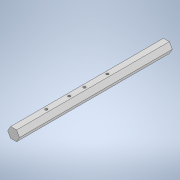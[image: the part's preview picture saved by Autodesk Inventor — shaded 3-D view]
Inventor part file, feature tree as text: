
AUTODESK INVENTOR PART (.ipt)
format: ipt  version: 2022 (Build 260153000, 153)  size: 123,392 bytes
history: native  units: mm
features: extrude x2, sketch x2
ambient origin geometry x8: Origin, YZ Plane, XZ Plane, XY Plane, X Axis, Y Axis, Z Axis, Center Point
bodies: Body1 (feature_tree)
feature tree (4):
  extrude  "Extrusion5"  Depth=3.1mm TaperAngle=360.0deg
  extrude  "Extrusion6"  Depth=80.0mm
  sketch  "Sketch5"  dims[d9=3.1mm d10=60.0mm d12=360.0deg]
  sketch  "Sketch6"  dims[d14=80.0mm d15=0.0mm d16=1.3mm d17=49.1mm d18=37.1mm d19=29.1mm d20=17.1mm d21=6.0mm d22=0.0mm]
